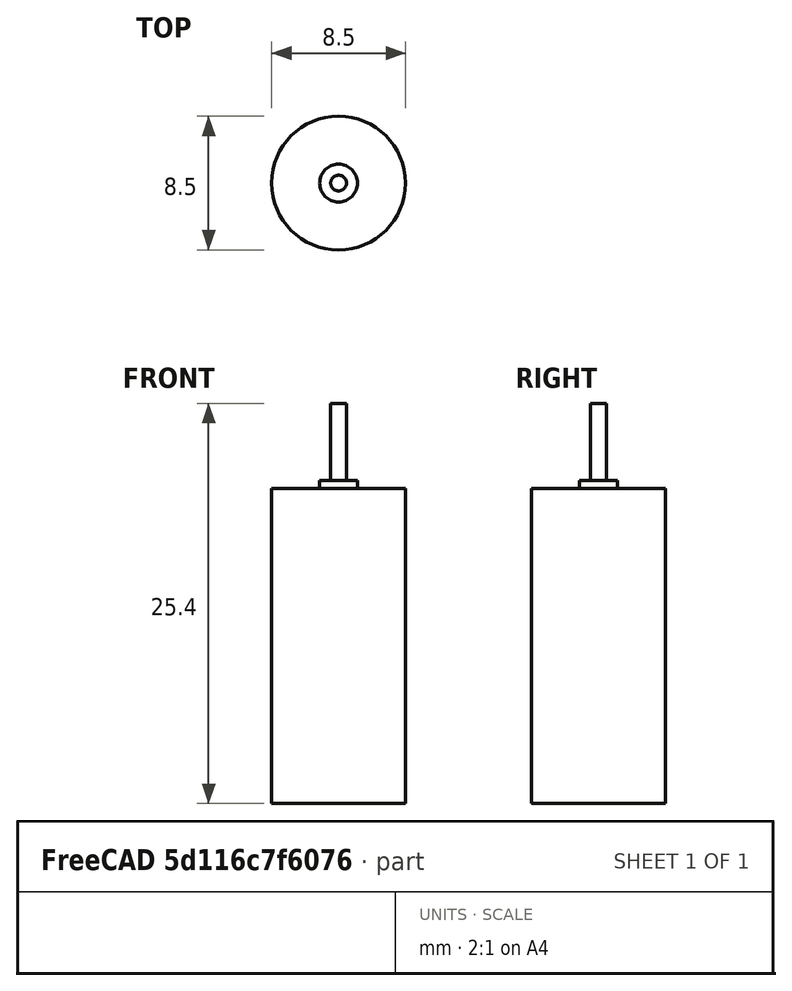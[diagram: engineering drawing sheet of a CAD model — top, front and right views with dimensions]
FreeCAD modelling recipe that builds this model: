
FCSTD DOCUMENT  (FreeCAD 0.16R6188 (Git))
Label: Motor-CC-3.3V-WlToy911
License: All rights reserved
LicenseURL: http://en.wikipedia.org/wiki/All_rights_reserved
objects: Sketcher::SketchObject×1, PartDesign::Revolution×1
note: 3 computed .brp shape members not serialized (recipe doc carries the construction recipe); baked Part::Feature solids carry a one-line shape summary decoded from their .brp

FEATURE [Sketcher::SketchObject] Sketch
  Placement = pos=(0,0,0) rot=(-1,0,0;4.71239rad)
  sketch-geometry (8):
    g0: LineSegment StartX=0 StartY=12.7 StartZ=0 EndX=0.5 EndY=12.7 EndZ=0
    g1: LineSegment StartX=0.5 StartY=12.7 StartZ=0 EndX=0.5 EndY=7.8 EndZ=0
    g2: LineSegment StartX=0.5 StartY=7.8 StartZ=0 EndX=1.2 EndY=7.8 EndZ=0
    g3: LineSegment StartX=1.2 StartY=7.8 StartZ=0 EndX=1.2 EndY=7.3 EndZ=0
    g4: LineSegment StartX=1.2 StartY=7.3 StartZ=0 EndX=4.25 EndY=7.3 EndZ=0
    g5: LineSegment StartX=4.25 StartY=7.3 StartZ=0 EndX=4.25 EndY=-12.7 EndZ=0
    g6: LineSegment StartX=4.25 StartY=-12.7 StartZ=0 EndX=0 EndY=-12.7 EndZ=0
    g7: LineSegment StartX=0 StartY=-12.7 StartZ=0 EndX=0 EndY=12.7 EndZ=0
  constraints (24):
    c: Coincident(g0,g1)
    c: Vertical(g1)
    c: Coincident(g1,g2)
    c: Horizontal(g2)
    c: Coincident(g2,g3)
    c: Vertical(g3)
    c: Coincident(g3,g4)
    c: Horizontal(g4)
    c: Coincident(g4,g5)
    c: Vertical(g5)
    c: Coincident(g5,g6)
    c: Horizontal(g6)
    c: Coincident(g6,g7)
    c: Vertical(g7)
    c: Horizontal(g0)
    c: Coincident(g0,g7)
    c: PointOnObject(g0,g-2)
    c: DistanceX(g0) = 0.5
    c: DistanceX(g2) = 1.2
    c: DistanceX(g4) = 4.25
    c: DistanceY(g7) = 25.4
    c: DistanceY(g1) = -4.9
    c: DistanceY(g3) = -0.5
    c: DistanceY(g0) = 12.7
FEATURE [PartDesign::Revolution] Revolution
  Angle = 360
  Axis = (0,0,1)
  Base = (0,0,0)
  Placement = pos=(0,0,0) rot=(-1,0,0;4.71239rad)
  ReferenceAxis = -> Sketch [V_Axis]
  Reversed = true
  Sketch = -> Sketch
